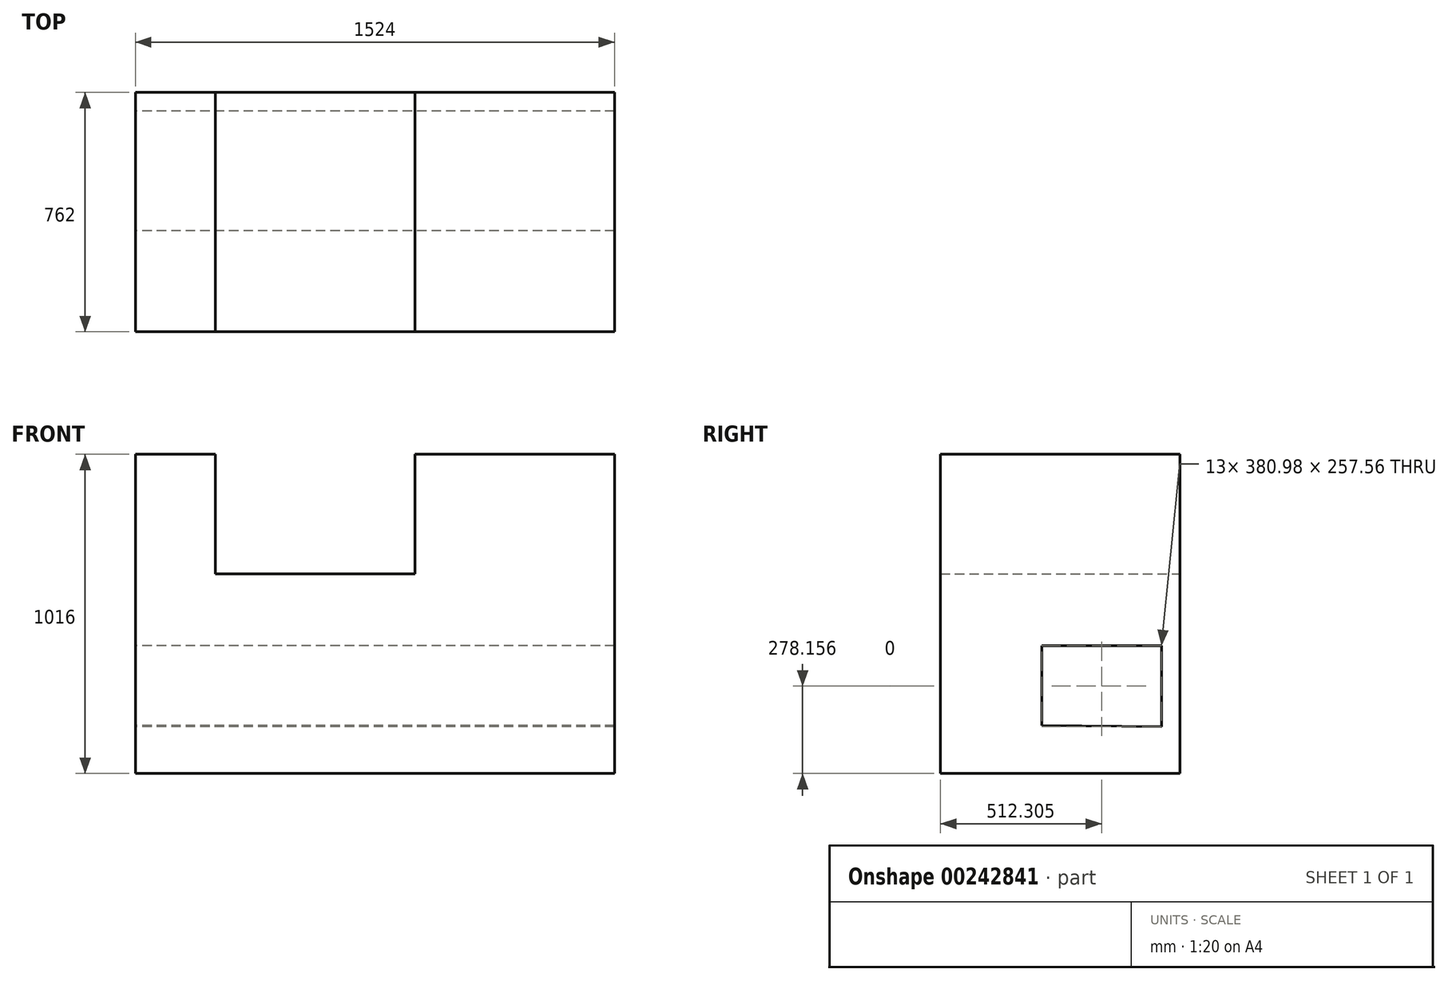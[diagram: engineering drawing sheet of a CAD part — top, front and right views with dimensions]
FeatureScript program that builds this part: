
annotation { "Feature Type Name" : "Feature", "Feature Type Description" : "" }
export const myFeature = defineFeature(function(context is Context, id is Id, definition is map)
    precondition{}
    {
        {
            var Q0;
            Q0=qCreatedBy(makeId("Front.planeOp"),FACE);
            var sketch = newSketch(context, id + "F0", { "sketchPlane" : qUnion([Q0])});
            skLineSegment(sketch, "E0", {"start": v(0, 0) * mm, "end": v(0, 1016) * mm});
            skLineSegment(sketch, "E1", {"start": v(0, 0) * mm, "end": v(-1524, 0) * mm});
            skLineSegment(sketch, "E2", {"start": v(-1524, 0) * mm, "end": v(-1524, 1016) * mm});
            skLineSegment(sketch, "E3", {"start": v(-1524, 1016) * mm, "end": v(-1270, 1016) * mm});
            skLineSegment(sketch, "E4", {"start": v(-1270, 1016) * mm, "end": v(-1270, 635) * mm});
            skLineSegment(sketch, "E5", {"start": v(-1270, 635) * mm, "end": v(-635, 635) * mm});
            skLineSegment(sketch, "E6", {"start": v(-635, 635) * mm, "end": v(-635, 1016) * mm});
            skLineSegment(sketch, "E7", {"start": v(-635, 1016) * mm, "end": v(0, 1016) * mm});
            skSolve(sketch);
        }
        {
            var Q0;
            Q0 = qSketchRegion(id + "F0", true);
            extrude(context, id + "F1", {"entities" : qUnion([Q0]), "depth" : 762 * mm});
        }
        {
            var Q0;
            Q0=makeQuery(id+"F1.opExtrude","SWEPT_FACE",FACE,{"disambiguationData":[OSD([sQuery(id+"F0.wireOp",EDGE,"E2")])]});
            var sketch = newSketch(context, id + "F2", { "sketchPlane" : qUnion([Q0])});
            skLineSegment(sketch, "E8", {"start": v(59.2, 149.38) * mm, "end": v(59.2, 406.94) * mm});
            skLineSegment(sketch, "E9", {"start": v(59.2, 406.94) * mm, "end": v(440.19, 406.94) * mm});
            skLineSegment(sketch, "E10", {"start": v(440.19, 406.94) * mm, "end": v(440.19, 152.94) * mm});
            skLineSegment(sketch, "E11", {"start": v(59.2, 149.38) * mm, "end": v(440.19, 152.94) * mm});
            skSolve(sketch);
        }
        {
            var Q0;
            Q0=makeQuery(id+"F2.imprint","IMPRINT",FACE,{"disambiguationData":[TD([[makeQuery(id+"F2.imprint","IMPRINT",EDGE,{"derivedFrom":sQuery(id+"F2.wireOp",EDGE,"E8")}),-1.0]])]});
            extrude(context, id + "F3", {"entities" : qUnion([Q0]), "operationType" : NewBodyOperationType.REMOVE, "endBound" : BoundingType.THROUGH_ALL, "oppositeDirection" : true, "depth" : 25.4 * mm});
        }
    });
